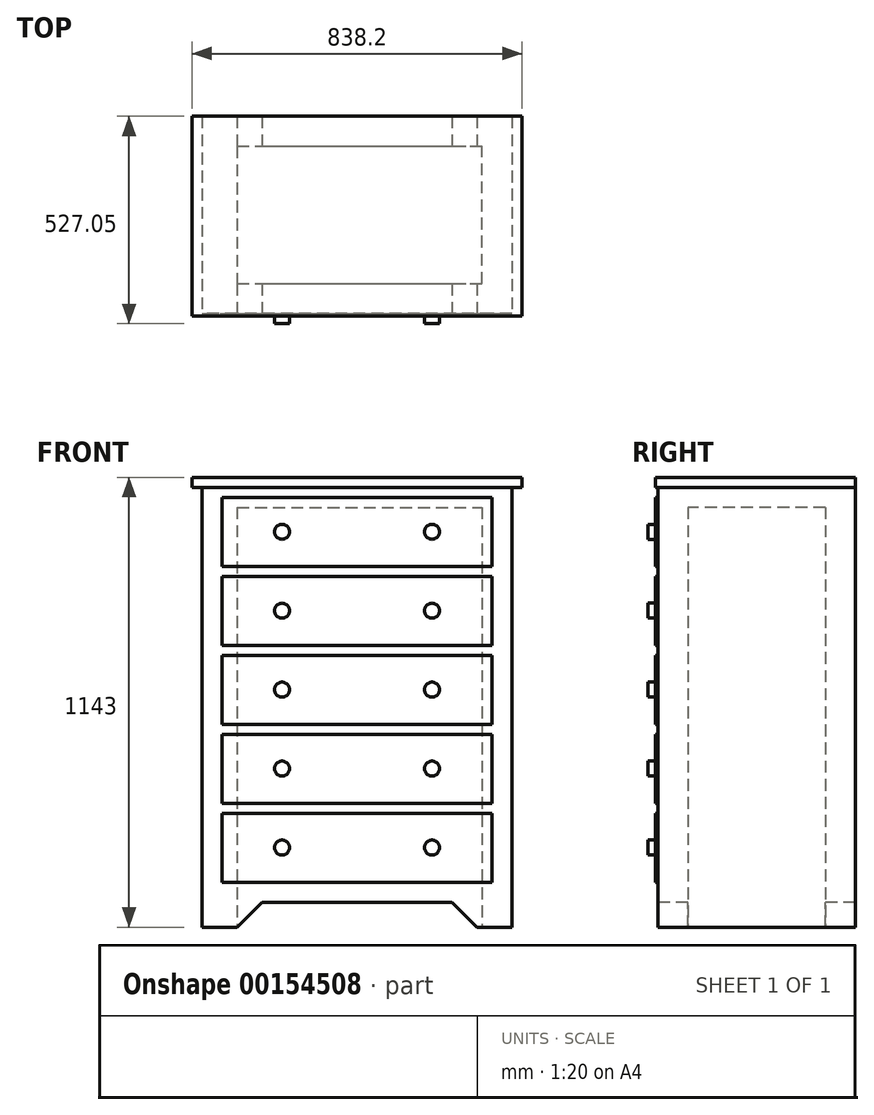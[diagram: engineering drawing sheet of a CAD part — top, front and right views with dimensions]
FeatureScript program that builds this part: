
annotation { "Feature Type Name" : "Feature", "Feature Type Description" : "" }
export const myFeature = defineFeature(function(context is Context, id is Id, definition is map)
    precondition{}
    {
        {
            var Q0;
            Q0=qCreatedBy(makeId("Top.planeOp"),FACE);
            var sketch = newSketch(context, id + "F0", { "sketchPlane" : qUnion([Q0])});
            skLineSegment(sketch, "E0.bottom", {"start": v(419.1, 254) * mm, "end": v(-419.1, 254) * mm});
            skLineSegment(sketch, "E0.top", {"start": v(419.1, -254) * mm, "end": v(-419.1, -254) * mm});
            skLineSegment(sketch, "E0.left", {"start": v(419.1, 254) * mm, "end": v(419.1, -254) * mm});
            skLineSegment(sketch, "E0.right", {"start": v(-419.1, 254) * mm, "end": v(-419.1, -254) * mm});
            skPoint(sketch, "E0.middle", {"position": v(0, 0) * mm});
            skSolve(sketch);
        }
        {
            var Q0;
            Q0=makeQuery(id+"F0.imprint","IMPRINT",FACE,{"disambiguationData":[TD([[makeQuery(id+"F0.imprint","IMPRINT",EDGE,{"derivedFrom":sQuery(id+"F0.wireOp",EDGE,"E0.bottom")}),1.0]])]});
            extrude(context, id + "F1", {"entities" : qUnion([Q0]), "depth" : 1143 * mm});
        }
        {
            var Q0;
            Q0=makeQuery(id+"F1.opExtrude","SWEPT_FACE",FACE,{"disambiguationData":[OSD([sQuery(id+"F0.wireOp",EDGE,"E0.top")])]});
            var sketch = newSketch(context, id + "F2", { "sketchPlane" : qUnion([Q0])});
            skLineSegment(sketch, "E1.bottom", {"start": v(-419.1, 0) * mm, "end": v(-393.7, 0) * mm});
            skLineSegment(sketch, "E1.top", {"start": v(-419.1, 1117.6) * mm, "end": v(-393.7, 1117.6) * mm});
            skLineSegment(sketch, "E1.left", {"start": v(-419.1, 0) * mm, "end": v(-419.1, 1117.6) * mm});
            skLineSegment(sketch, "E1.right", {"start": v(-393.7, 0) * mm, "end": v(-393.7, 1117.6) * mm});
            skLineSegment(sketch, "E2.bottom", {"start": v(419.1, 0) * mm, "end": v(393.7, 0) * mm});
            skLineSegment(sketch, "E2.top", {"start": v(419.1, 1117.6) * mm, "end": v(393.7, 1117.6) * mm});
            skLineSegment(sketch, "E2.left", {"start": v(419.1, 0) * mm, "end": v(419.1, 1117.6) * mm});
            skLineSegment(sketch, "E2.right", {"start": v(393.7, 0) * mm, "end": v(393.7, 1117.6) * mm});
            skLineSegment(sketch, "E3", {"start": v(-304.8, 0) * mm, "end": v(-241.3, 63.5) * mm});
            skLineSegment(sketch, "E4", {"start": v(-241.3, 63.5) * mm, "end": v(241.3, 63.5) * mm});
            skLineSegment(sketch, "E5", {"start": v(241.3, 63.5) * mm, "end": v(304.8, 0) * mm});
            skLineSegment(sketch, "E6", {"start": v(304.8, 0) * mm, "end": v(-304.8, 0) * mm});
            skLineSegment(sketch, "E7.bottom", {"start": v(-342.9, 1092.2) * mm, "end": v(342.9, 1092.2) * mm});
            skLineSegment(sketch, "E7.top", {"start": v(-342.9, 916.94) * mm, "end": v(342.9, 916.94) * mm});
            skLineSegment(sketch, "E7.left", {"start": v(-342.9, 1092.2) * mm, "end": v(-342.9, 916.94) * mm});
            skLineSegment(sketch, "E7.right", {"start": v(342.9, 1092.2) * mm, "end": v(342.9, 916.94) * mm});
            skLineSegment(sketch, "E8.bottom", {"start": v(342.9, 891.54) * mm, "end": v(-342.9, 891.54) * mm});
            skLineSegment(sketch, "E8.top", {"start": v(342.9, 716.28) * mm, "end": v(-342.9, 716.28) * mm});
            skLineSegment(sketch, "E8.left", {"start": v(342.9, 891.54) * mm, "end": v(342.9, 716.28) * mm});
            skLineSegment(sketch, "E8.right", {"start": v(-342.9, 891.54) * mm, "end": v(-342.9, 716.28) * mm});
            skLineSegment(sketch, "E9.bottom", {"start": v(342.9, 690.88) * mm, "end": v(-342.9, 690.88) * mm});
            skLineSegment(sketch, "E9.top", {"start": v(342.9, 515.62) * mm, "end": v(-342.9, 515.62) * mm});
            skLineSegment(sketch, "E9.left", {"start": v(342.9, 690.88) * mm, "end": v(342.9, 515.62) * mm});
            skLineSegment(sketch, "E9.right", {"start": v(-342.9, 690.88) * mm, "end": v(-342.9, 515.62) * mm});
            skLineSegment(sketch, "E10.bottom", {"start": v(342.9, 490.22) * mm, "end": v(-342.9, 490.22) * mm});
            skLineSegment(sketch, "E10.top", {"start": v(342.9, 314.96) * mm, "end": v(-342.9, 314.96) * mm});
            skLineSegment(sketch, "E10.left", {"start": v(342.9, 490.22) * mm, "end": v(342.9, 314.96) * mm});
            skLineSegment(sketch, "E10.right", {"start": v(-342.9, 490.22) * mm, "end": v(-342.9, 314.96) * mm});
            skLineSegment(sketch, "E11.bottom", {"start": v(342.9, 289.56) * mm, "end": v(-342.9, 289.56) * mm});
            skLineSegment(sketch, "E11.top", {"start": v(342.9, 114.3) * mm, "end": v(-342.9, 114.3) * mm});
            skLineSegment(sketch, "E11.left", {"start": v(342.9, 289.56) * mm, "end": v(342.9, 114.3) * mm});
            skLineSegment(sketch, "E11.right", {"start": v(-342.9, 289.56) * mm, "end": v(-342.9, 114.3) * mm});
            skLineSegment(sketch, "E12", {"start": v(0, 916.94) * mm, "end": v(0, 891.54) * mm, "construction": true});
            skLineSegment(sketch, "E13", {"start": v(0, 716.28) * mm, "end": v(0, 690.88) * mm, "construction": true});
            skLineSegment(sketch, "E14", {"start": v(0, 515.62) * mm, "end": v(0, 490.22) * mm, "construction": true});
            skLineSegment(sketch, "E15", {"start": v(0, 314.96) * mm, "end": v(0, 289.56) * mm, "construction": true});
            skLineSegment(sketch, "E16", {"start": v(-342.9, 1004.57) * mm, "end": v(-190.5, 1004.57) * mm, "construction": true});
            skLineSegment(sketch, "E17", {"start": v(-190.5, 1004.57) * mm, "end": v(190.5, 1004.57) * mm, "construction": true});
            skLineSegment(sketch, "E18", {"start": v(190.5, 1004.57) * mm, "end": v(342.9, 1004.57) * mm, "construction": true});
            skCircle(sketch, "E19", {"center": v(-190.5, 1004.57) * mm, "radius": 19.05 * mm});
            skCircle(sketch, "E20", {"center": v(190.5, 1004.57) * mm, "radius": 19.05 * mm});
            skLineSegment(sketch, "E21", {"start": v(-342.9, 803.9) * mm, "end": v(-239.56, 803.9) * mm, "construction": true});
            skCircle(sketch, "E22.0.1.0", {"center": v(-190.5, 804.01) * mm, "radius": 19.05 * mm});
            skCircle(sketch, "E22.0.1.1", {"center": v(190.5, 804.01) * mm, "radius": 19.05 * mm});
            skCircle(sketch, "E22.0.2.0", {"center": v(-190.5, 603.45) * mm, "radius": 19.05 * mm});
            skCircle(sketch, "E22.0.2.1", {"center": v(190.5, 603.45) * mm, "radius": 19.05 * mm});
            skCircle(sketch, "E22.0.3.0", {"center": v(-190.5, 402.9) * mm, "radius": 19.05 * mm});
            skCircle(sketch, "E22.0.3.1", {"center": v(190.5, 402.9) * mm, "radius": 19.05 * mm});
            skCircle(sketch, "E22.0.4.0", {"center": v(-190.5, 202.34) * mm, "radius": 19.05 * mm});
            skCircle(sketch, "E22.0.4.1", {"center": v(190.5, 202.34) * mm, "radius": 19.05 * mm});
            skLineSegment(sketch, "E22.direction1", {"start": v(-190.5, 1004.57) * mm, "end": v(-165.5, 1004.57) * mm, "construction": true});
            skLineSegment(sketch, "E22.direction2", {"start": v(-190.5, 1004.57) * mm, "end": v(-190.5, 804.01) * mm, "construction": true});
            skLineSegment(sketch, "E23", {"start": v(-393.7, 1117.6) * mm, "end": v(393.7, 1117.6) * mm});
            skSolve(sketch);
        }
        {
            var Q0;
            Q0=makeQuery(id+"F2.imprint","IMPRINT",FACE,{"disambiguationData":[TD([[makeQuery(id+"F2.imprint","IMPRINT",EDGE,{"derivedFrom":sQuery(id+"F2.wireOp",EDGE,"E1.bottom")}),-1.0]])]});
            var Q1;
            Q1=makeQuery(id+"F2.imprint","IMPRINT",FACE,{"disambiguationData":[TD([[makeQuery(id+"F2.imprint","IMPRINT",EDGE,{"derivedFrom":sQuery(id+"F2.wireOp",EDGE,"E2.bottom")}),-1.0]])]});
            var Q2;
            Q2=makeQuery(id+"F2.imprint","IMPRINT",FACE,{"disambiguationData":[TD([[makeQuery(id+"F2.imprint","IMPRINT",EDGE,{"derivedFrom":sQuery(id+"F2.wireOp",EDGE,"E3")}),-1.0]])]});
            extrude(context, id + "F3", {"entities" : qUnion([Q0, Q1, Q2]), "operationType" : NewBodyOperationType.REMOVE, "endBound" : BoundingType.THROUGH_ALL, "oppositeDirection" : true, "depth" : 30.48 * mm});
        }
        {
            var Q0;
            {var subQ0=sQuery(id+"F2.wireOp",EDGE,"E1.right");Q0=makeQuery(id+"F2.imprint","IMPRINT",FACE,{"disambiguationData":[TD([[makeQuery(id+"F2.imprint","IMPRINT",EDGE,{"derivedFrom":subQ0}),-1.0]])]});}
            extrude(context, id + "F4", {"entities" : qUnion([Q0]), "operationType" : NewBodyOperationType.REMOVE, "oppositeDirection" : true, "depth" : 6.35 * mm});
        }
        {
            var Q0;
            Q0=makeQuery(id+"F2.imprint","IMPRINT",FACE,{"disambiguationData":[TD([[makeQuery(id+"F2.imprint","IMPRINT",EDGE,{"derivedFrom":sQuery(id+"F2.wireOp",EDGE,"E19")}),1.0]])]});
            var Q1;
            Q1=makeQuery(id+"F2.imprint","IMPRINT",FACE,{"disambiguationData":[TD([[makeQuery(id+"F2.imprint","IMPRINT",EDGE,{"derivedFrom":sQuery(id+"F2.wireOp",EDGE,"E20")}),1.0]])]});
            var Q2;
            Q2=makeQuery(id+"F2.imprint","IMPRINT",FACE,{"disambiguationData":[TD([[makeQuery(id+"F2.imprint","IMPRINT",EDGE,{"derivedFrom":sQuery(id+"F2.wireOp",EDGE,"E22.0.1.1")}),1.0]])]});
            var Q3;
            Q3=makeQuery(id+"F2.imprint","IMPRINT",FACE,{"disambiguationData":[TD([[makeQuery(id+"F2.imprint","IMPRINT",EDGE,{"derivedFrom":sQuery(id+"F2.wireOp",EDGE,"E22.0.1.0")}),1.0]])]});
            var Q4;
            Q4=makeQuery(id+"F2.imprint","IMPRINT",FACE,{"disambiguationData":[TD([[makeQuery(id+"F2.imprint","IMPRINT",EDGE,{"derivedFrom":sQuery(id+"F2.wireOp",EDGE,"E22.0.2.0")}),1.0]])]});
            var Q5;
            Q5=makeQuery(id+"F2.imprint","IMPRINT",FACE,{"disambiguationData":[TD([[makeQuery(id+"F2.imprint","IMPRINT",EDGE,{"derivedFrom":sQuery(id+"F2.wireOp",EDGE,"E22.0.2.1")}),1.0]])]});
            var Q6;
            Q6=makeQuery(id+"F2.imprint","IMPRINT",FACE,{"disambiguationData":[TD([[makeQuery(id+"F2.imprint","IMPRINT",EDGE,{"derivedFrom":sQuery(id+"F2.wireOp",EDGE,"E22.0.3.1")}),1.0]])]});
            var Q7;
            Q7=makeQuery(id+"F2.imprint","IMPRINT",FACE,{"disambiguationData":[TD([[makeQuery(id+"F2.imprint","IMPRINT",EDGE,{"derivedFrom":sQuery(id+"F2.wireOp",EDGE,"E22.0.3.0")}),1.0]])]});
            var Q8;
            Q8=makeQuery(id+"F2.imprint","IMPRINT",FACE,{"disambiguationData":[TD([[makeQuery(id+"F2.imprint","IMPRINT",EDGE,{"derivedFrom":sQuery(id+"F2.wireOp",EDGE,"E22.0.4.0")}),1.0]])]});
            var Q9;
            Q9=makeQuery(id+"F2.imprint","IMPRINT",FACE,{"disambiguationData":[TD([[makeQuery(id+"F2.imprint","IMPRINT",EDGE,{"derivedFrom":sQuery(id+"F2.wireOp",EDGE,"E22.0.4.1")}),1.0]])]});
            extrude(context, id + "F5", {"entities" : qUnion([Q0, Q1, Q2, Q3, Q4, Q5, Q6, Q7, Q8, Q9]), "operationType" : NewBodyOperationType.ADD, "depth" : 19.05 * mm});
        }
        {
            var Q0;
            {var subQ0=sQuery(id+"F0.wireOp",EDGE,"E0.bottom");var subQ1=sQuery(id+"F0.wireOp",EDGE,"E0.top");Q0=makeQuery(id+"F3.boolean.opBoolean","SPLIT",FACE,{"disambiguationData":[TD([makeQuery(id+"F3.opExtrude","SWEPT_FACE",FACE,{"disambiguationData":[OSD([sQuery(id+"F2.wireOp",EDGE,"E1.right")])]})])],"derivedFrom":makeQuery(id+"F1.opExtrude","CAP_FACE",FACE,{"disambiguationData":[OSD([subQ0,subQ1,sQuery(id+"F0.wireOp",EDGE,"E0.left"),sQuery(id+"F0.wireOp",EDGE,"E0.right")])],"isStart":true})});}
            var sketch = newSketch(context, id + "F6", { "sketchPlane" : qUnion([Q0])});
            skLineSegment(sketch, "E24.bottom", {"start": v(-317.5, 171.45) * mm, "end": v(317.5, 171.45) * mm});
            skLineSegment(sketch, "E24.top", {"start": v(-317.5, -177.8) * mm, "end": v(317.5, -177.8) * mm});
            skLineSegment(sketch, "E24.left", {"start": v(-317.5, 171.45) * mm, "end": v(-317.5, -177.8) * mm});
            skLineSegment(sketch, "E24.right", {"start": v(317.5, 171.45) * mm, "end": v(317.5, -177.8) * mm});
            skSolve(sketch);
        }
        {
            var Q0;
            {var subQ0=sQuery(id+"F6.wireOp",EDGE,"E24.right");Q0=makeQuery(id+"F6.imprint","IMPRINT",FACE,{"disambiguationData":[TD([[makeQuery(id+"F6.imprint","IMPRINT",EDGE,{"derivedFrom":subQ0}),-1.0]])]});}
            extrude(context, id + "F7", {"entities" : qUnion([Q0]), "operationType" : NewBodyOperationType.REMOVE, "oppositeDirection" : true, "depth" : 1066.8 * mm});
        }
    });
